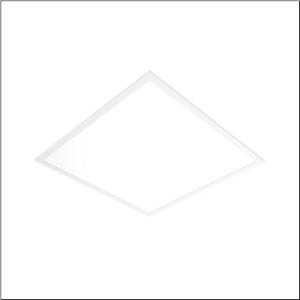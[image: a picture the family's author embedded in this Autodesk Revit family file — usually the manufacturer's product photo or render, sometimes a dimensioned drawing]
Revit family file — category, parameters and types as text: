
# Revit family: apollon_r__41_51mh11w72m43_60bb
name_source: partatom
category: Lighting Fixtures
units: mm (PartAtom-declared; Revit-internal decimal feet)

## family parameters
Cut with Voids When Loaded = No
Host = Face
Light Source = No
Part Type = Normal
Room Calculation Point = No
Round Connector Dimension = Use Diameter
Shared = No

## types (1)
- --- (1 x LED, 3700 lm, 28.5 W, 4000K)
    Apparent Load = 29 VA
    CIE Flux Codes = 61 87 97 100 100
    Color Rendering = 80
    Color Temperature = 4000K
    Default Elevation = 1800 mm
    Description = Apollon® 41, office luminaire, primary optical cover: prismatic diffuser, of PS, light emission: direct distribution, primary light characteristic: symmetric, installation type: lay-in mounting, LED, rated luminous flux: 3.700lm, luminous efficacy: 130lm/W, light colour: 830/840, colour temperature: 3000/4000K, with terminal, 3-pole, mains connection: 220..240V, AC, 50/60Hz, housing, of aluminium section, traffic white (RAL 9016), module: M625, length: 620mm, width: 620mm, height: 28mm, housing upper side, of sheet steel, protection rating (complete): IP20, protection rating (lamp compartment, on room side): IP40, insulation class (complete): insulation class II (safety insulation), certification: CE, ENEC, permissible operating ambient temperature: -25..+40°C, packaging unit: 1 piece
    Height = 0 mm  [stored 0 ft]
    Lamp = 1 x LED
    Lamp Light Flux = 3700 lm
    Lamp Power = 28.5 W
    Lamp count = 1
    Length = 620 mm
    Luminous efficacy = 130 lm/W
    Manufacturer = Siteco
    ModVariant = No
    Model = 51MH11W72M43
    Mounting Place = Ceiling
    Mounting Type = Recessed
    Number of Poles = 1
    OnlyDefault = Yes
    Power Factor = 1
    Product Name = Apollon® 41
    Product group = office luminaire | ceiling recessed
    ProductGroupID = 401
    Protection Class = Protection class II
    Protection Degree = IP 20
    RLX_Detail_Level = 1
    RLX_Emergency_Light_Flux = 0 lm
    RLX_Emergency_Type = 0
    RLX_Emergency_Type_DB = No
    RlxData = <blob elided: 12397 chars, md5=81992a79>
    Socket = socket
    Standby Power = 0 W
    System Light Flux = 3700 lm
    System Power = 29 W
    Type Comments = factory setting
    Type Image = l_1291024.jpg
    URL = http://relux.com
    VarID = @adj_008963
    Voltage = 0 V
    Weight = 0.00 kg
    Width = 620 mm

note: [stored X ft] marks values corroborated as IEEE doubles in the binary element streams (Revit-internal decimal feet)

## geometry (parser evidence)
native form markers: Sweep x11
no freeform markers — native parametric forms only
